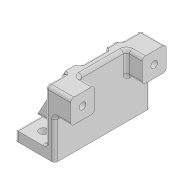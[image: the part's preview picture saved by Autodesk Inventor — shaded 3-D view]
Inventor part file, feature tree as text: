
AUTODESK INVENTOR PART (.ipt)
format: ipt  version: 2020 (Build 240168000, 168)  size: 368,128 bytes
history: native  units: mm
features: extrude x7, sketch x7, chamfer x2, other x1, fillet x1
ambient origin geometry x8: Origin, YZ Plane, XZ Plane, XY Plane, X Axis, Y Axis, Z Axis, Center Point
bodies: Body1 (feature_tree)
feature tree (18):
  other  "Sólido1"
  extrude  "Extrusão1"  Depth=40.0mm
  extrude  "Extrusão2"  Depth=6.0mm
  extrude  "Extrusão3"  Depth=40.0mm TaperAngle=0.0deg
  extrude  "Extrusão4"  TaperAngle=0.0deg  [1 undecoded]
  extrude  "Extrusão5"  Depth=15.0mm
  extrude  "Extrusão6"  Depth=4.2mm
  extrude  "Extrusão7"  Depth=10.0mm TaperAngle=0.0deg
  chamfer  "Chanfro2"  Distance=7.5mm
  chamfer  "Chanfro3"  Distance=7.5mm
  fillet  "Arredondamento1"  Radius=7.5mm
  sketch  "Esboço1"  dims[d0=25.0mm d1=40.0mm]
  sketch  "Esboço2"  dims[d2=60.0mm d3=0.0mm d4=6.0mm]
  sketch  "Esboço3"  dims[d5=6.0mm d6=40.0mm d7=0.0mm]
  sketch  "Esboço4"  dims[d8=15.0mm d9=0.0mm]
  sketch  "Esboço5"  dims[d10=0.0mm d11=15.0mm]
  sketch  "Esboço6"  dims[d12=15.0mm d13=4.2mm]
  sketch  "Esboço7"  dims[d14=4.2mm d15=10.0mm d16=0.0mm d17=7.5mm d18=7.5mm d19=7.5mm d20=7.5mm d21=50.0mm d22=0.0mm d23=6.9mm d24=6.9mm d25=6.0mm d26=0.0mm d27=5.3mm d28=5.3mm d29=8.0mm d30=8.0mm d31=10.0mm d32=0.0mm d33=6.0mm d34=6.0mm d35=14.0mm d36=14.0mm d37=19.0mm d38=0.0mm d42=33.0mm d43=18.0mm d44=45.0deg d45=33.0mm d46=18.0mm d47=45.0deg d48=2.0mm]
note: 1 required parameter value undecoded (feature->parameter linkage not recoverable at this tier; creation-order binding heuristic only, values carry confidence <= 0.55)
